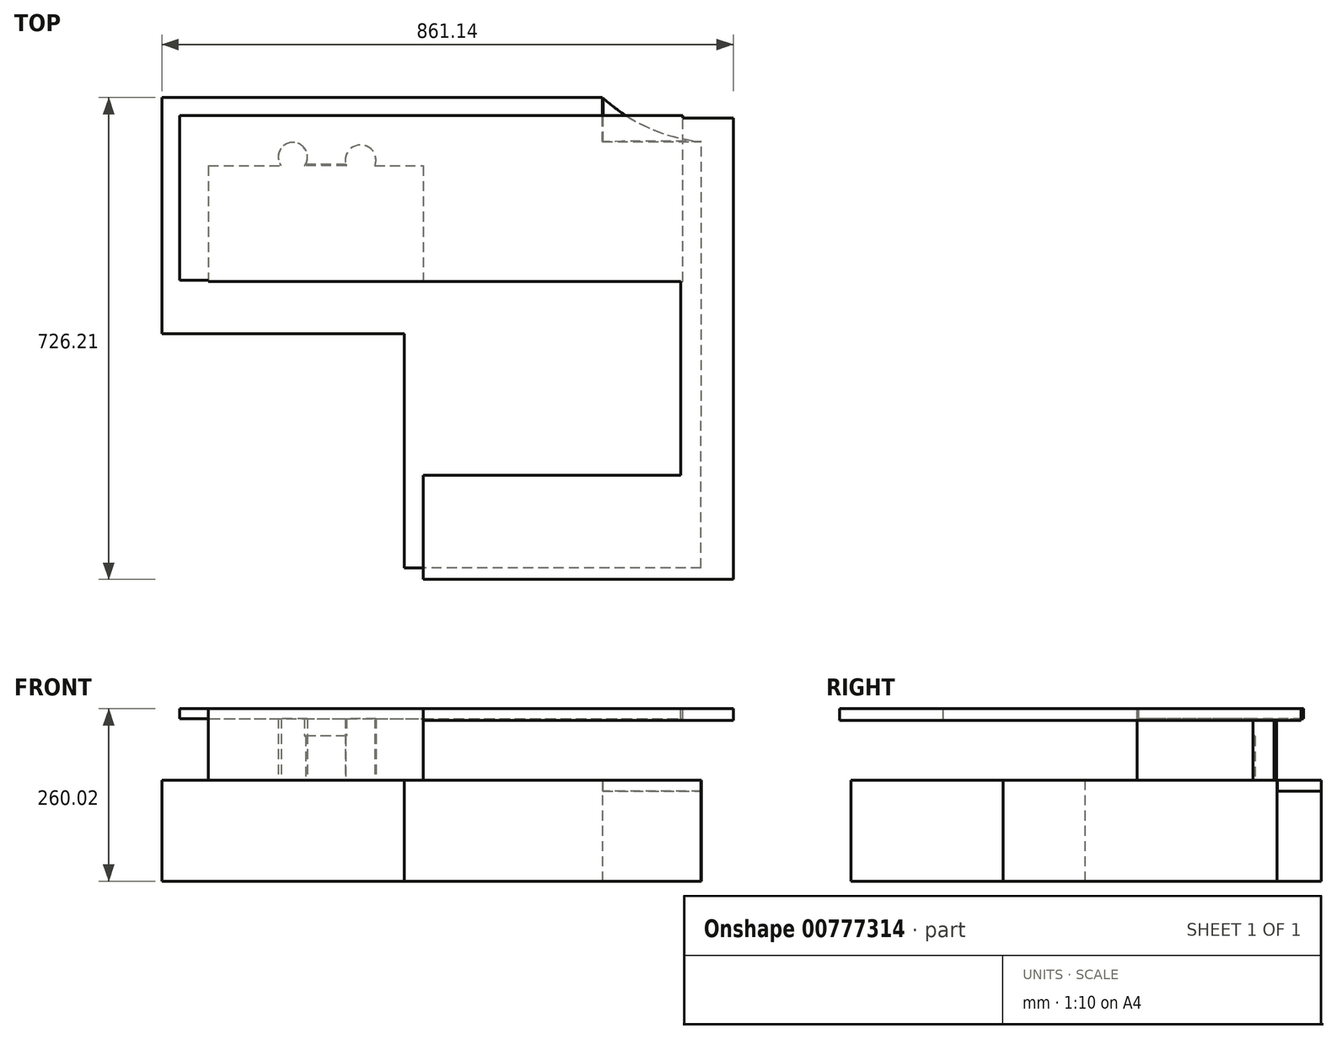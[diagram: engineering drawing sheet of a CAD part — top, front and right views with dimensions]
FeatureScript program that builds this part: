
annotation { "Feature Type Name" : "Feature", "Feature Type Description" : "" }
export const myFeature = defineFeature(function(context is Context, id is Id, definition is map)
    precondition{}
    {
        {
            var Q0;
            Q0=qCreatedBy(makeId("Top.planeOp"),FACE);
            var sketch = newSketch(context, id + "F0", { "sketchPlane" : qUnion([Q0])});
            skLineSegment(sketch, "E0.bottom", {"start": v(-322.14, 356.23) * mm, "end": v(-103.37, 356.23) * mm});
            skLineSegment(sketch, "E0.top", {"start": v(-322.14, 0) * mm, "end": v(-103.37, 0) * mm});
            skLineSegment(sketch, "E0.left", {"start": v(-322.14, 356.23) * mm, "end": v(-322.14, 0) * mm});
            skLineSegment(sketch, "E0.right", {"start": v(-103.37, 356.23) * mm, "end": v(-103.37, 0) * mm});
            skLineSegment(sketch, "E1.bottom", {"start": v(-103.37, 0) * mm, "end": v(193.48, 0) * mm});
            skLineSegment(sketch, "E1.top", {"start": v(-103.37, 139.09) * mm, "end": v(193.48, 139.09) * mm});
            skLineSegment(sketch, "E1.left", {"start": v(-103.37, 0) * mm, "end": v(-103.37, 139.09) * mm});
            skLineSegment(sketch, "E1.right", {"start": v(193.48, 0) * mm, "end": v(193.48, 139.09) * mm});
            skLineSegment(sketch, "E2.bottom", {"start": v(193.48, 0) * mm, "end": v(43.02, 0) * mm});
            skLineSegment(sketch, "E2.top", {"start": v(193.48, -352.95) * mm, "end": v(43.02, -352.95) * mm});
            skLineSegment(sketch, "E2.left", {"start": v(193.48, 0) * mm, "end": v(193.48, -352.95) * mm});
            skLineSegment(sketch, "E2.right", {"start": v(43.02, 0) * mm, "end": v(43.02, -352.95) * mm});
            skLineSegment(sketch, "E3.bottom", {"start": v(193.48, -352.95) * mm, "end": v(490.32, -352.95) * mm});
            skLineSegment(sketch, "E3.top", {"start": v(193.48, -123.6) * mm, "end": v(490.32, -123.6) * mm});
            skLineSegment(sketch, "E3.left", {"start": v(193.48, -352.95) * mm, "end": v(193.48, -123.6) * mm});
            skLineSegment(sketch, "E3.right", {"start": v(490.32, -352.95) * mm, "end": v(490.32, -123.6) * mm});
            skLineSegment(sketch, "E4.bottom", {"start": v(341.9, -123.6) * mm, "end": v(491.14, -123.6) * mm});
            skLineSegment(sketch, "E4.top", {"start": v(341.9, 289.54) * mm, "end": v(491.14, 289.54) * mm});
            skLineSegment(sketch, "E4.left", {"start": v(341.9, -123.6) * mm, "end": v(341.9, 289.54) * mm});
            skLineSegment(sketch, "E4.right", {"start": v(491.14, -123.6) * mm, "end": v(491.14, 289.54) * mm});
            skLineSegment(sketch, "E5.bottom", {"start": v(341.9, 289.54) * mm, "end": v(-103.37, 289.54) * mm});
            skLineSegment(sketch, "E5.top", {"start": v(341.9, 356.23) * mm, "end": v(-103.37, 356.23) * mm});
            skLineSegment(sketch, "E5.left", {"start": v(341.9, 289.54) * mm, "end": v(341.9, 356.23) * mm});
            skLineSegment(sketch, "E5.right", {"start": v(-103.37, 289.54) * mm, "end": v(-103.37, 356.23) * mm});
            skSolve(sketch);
        }
        {
            var Q0;
            {var subQ5=sQuery(id+"F0.wireOp",EDGE,"E1.top");Q0=makeQuery(id+"F0.imprint","IMPRINT",FACE,{"disambiguationData":[TD([[makeQuery(id+"F0.imprint","IMPRINT",EDGE,{"derivedFrom":subQ5}),1.0]])]});}
            var Q1;
            {var subQ0=sQuery(id+"F0.wireOp",EDGE,"E1.top");Q1=makeQuery(id+"F0.imprint","IMPRINT",FACE,{"disambiguationData":[TD([[makeQuery(id+"F0.imprint","IMPRINT",EDGE,{"derivedFrom":subQ0}),-1.0]])]});}
            var Q2;
            {var subQ4=sQuery(id+"F0.wireOp",EDGE,"E2.top");Q2=makeQuery(id+"F0.imprint","IMPRINT",FACE,{"disambiguationData":[TD([[makeQuery(id+"F0.imprint","IMPRINT",EDGE,{"derivedFrom":subQ4}),-1.0]])]});}
            var Q3;
            {var subQ3=sQuery(id+"F0.wireOp",EDGE,"E3.bottom");Q3=makeQuery(id+"F0.imprint","IMPRINT",FACE,{"disambiguationData":[TD([[makeQuery(id+"F0.imprint","IMPRINT",EDGE,{"derivedFrom":subQ3}),1.0]])]});}
            var Q4;
            {var subQ0=sQuery(id+"F0.wireOp",EDGE,"E4.bottom");Q4=makeQuery(id+"F0.imprint","IMPRINT",FACE,{"disambiguationData":[TD([[makeQuery(id+"F0.imprint","IMPRINT",EDGE,{"derivedFrom":subQ0}),1.0]])]});}
            var Q5;
            {var subQ2=sQuery(id+"F0.wireOp",EDGE,"E5.bottom");Q5=makeQuery(id+"F0.imprint","IMPRINT",FACE,{"disambiguationData":[TD([[makeQuery(id+"F0.imprint","IMPRINT",EDGE,{"derivedFrom":subQ2}),-1.0]])]});}
            var Q6;
            {var subQ4=sQuery(id+"F0.wireOp",EDGE,"E0.bottom");Q6=makeQuery(id+"F0.imprint","IMPRINT",FACE,{"disambiguationData":[TD([[makeQuery(id+"F0.imprint","IMPRINT",EDGE,{"derivedFrom":subQ4}),-1.0]])]});}
            extrude(context, id + "F1", {"entities" : qUnion([Q0, Q1, Q2, Q3, Q4, Q5, Q6]), "depth" : 152.4 * mm, "offsetDistance" : 25.4 * mm});
        }
        {
            var Q0;
            Q0=makeQuery(id+"F1.opExtrude","CAP_FACE",FACE,{"disambiguationData":[OSD([sQuery(id+"F0.wireOp",EDGE,"E0.bottom"),sQuery(id+"F0.wireOp",EDGE,"E0.top"),sQuery(id+"F0.wireOp",EDGE,"E0.left"),sQuery(id+"F0.wireOp",EDGE,"E1.bottom"),sQuery(id+"F0.wireOp",EDGE,"E2.top"),sQuery(id+"F0.wireOp",EDGE,"E2.right"),sQuery(id+"F0.wireOp",EDGE,"E3.bottom"),sQuery(id+"F0.wireOp",EDGE,"E3.right"),sQuery(id+"F0.wireOp",EDGE,"E4.bottom"),sQuery(id+"F0.wireOp",EDGE,"E4.top"),sQuery(id+"F0.wireOp",EDGE,"E4.right"),sQuery(id+"F0.wireOp",EDGE,"E5.top"),sQuery(id+"F0.wireOp",EDGE,"E5.left")])],"isStart":false});
            var sketch = newSketch(context, id + "F2", { "sketchPlane" : qUnion([Q0])});
            skSolve(sketch);
        }
        {
            var Q0;
            Q0=makeQuery(id+"F2.imprint","IMPRINT",FACE,{"disambiguationData":[TD([[makeQuery(id+"F2.imprint","IMPRINT",EDGE,{"derivedFrom":makeQuery(id+"F1.opExtrude","CAP_EDGE",EDGE,{"disambiguationData":[OSD([sQuery(id+"F0.wireOp",EDGE,"E0.left")])],"isStart":false})}),1.0]])]});
            var sketch = newSketch(context, id + "F3", { "sketchPlane" : qUnion([Q0])});
            skArc(sketch, "E6", {"start": v(342.5, 355.85) * mm, "mid": v(411.41, 310.78) * mm, "end": v(491.05, 289.87) * mm});
            skArc(sketch, "E7", {"start": v(491.05, 289.87) * mm, "mid": v(417.06, 290.34) * mm, "end": v(343.06, 289.87) * mm});
            skArc(sketch, "E8", {"start": v(343.06, 289.87) * mm, "mid": v(343.13, 322.86) * mm, "end": v(342.5, 355.85) * mm});
            skSolve(sketch);
        }
        {
            var Q0;
            Q0=makeQuery(id+"F3.imprint","IMPRINT",FACE,{"disambiguationData":[TD([[makeQuery(id+"F3.imprint","IMPRINT",EDGE,{"derivedFrom":sQuery(id+"F3.wireOp",EDGE,"E6")}),-1.0]])]});
            extrude(context, id + "F4", {"entities" : qUnion([Q0]), "oppositeDirection" : true, "depth" : 16.5 * mm, "offsetDistance" : 25.4 * mm});
        }
        {
            var Q0;
            Q0=makeQuery(id+"F2.imprint","IMPRINT",FACE,{"disambiguationData":[TD([[makeQuery(id+"F2.imprint","IMPRINT",EDGE,{"derivedFrom":makeQuery(id+"F1.opExtrude","CAP_EDGE",EDGE,{"disambiguationData":[OSD([sQuery(id+"F0.wireOp",EDGE,"E0.left")])],"isStart":false})}),1.0]])]});
            var sketch = newSketch(context, id + "F5", { "sketchPlane" : qUnion([Q0])});
            skCircle(sketch, "E9", {"center": v(-124.59, 266.64) * mm, "radius": 21.98 * mm});
            skPoint(sketch, "E9.first.point", {"position": v(-131.84, 245.89) * mm});
            skPoint(sketch, "E9.second.point", {"position": v(-104.8, 257.08) * mm});
            skPoint(sketch, "E9.third.point", {"position": v(-142.1, 253.34) * mm});
            skCircle(sketch, "E10", {"center": v(-22.56, 261.86) * mm, "radius": 23.06 * mm});
            skPoint(sketch, "E10.first.point", {"position": v(0, 266.64) * mm});
            skPoint(sketch, "E10.second.point", {"position": v(-45.12, 257.08) * mm});
            skPoint(sketch, "E10.third.point", {"position": v(0, 257.08) * mm});
            skLineSegment(sketch, "E11", {"start": v(-251.84, 253.34) * mm, "end": v(-142.1, 253.34) * mm});
            skLineSegment(sketch, "E12.bottom", {"start": v(-251.84, 253.34) * mm, "end": v(71.57, 253.34) * mm});
            skLineSegment(sketch, "E12.top", {"start": v(-251.84, 78.78) * mm, "end": v(71.57, 78.78) * mm});
            skLineSegment(sketch, "E12.left", {"start": v(-251.84, 253.34) * mm, "end": v(-251.84, 78.78) * mm});
            skLineSegment(sketch, "E12.right", {"start": v(71.57, 253.34) * mm, "end": v(71.57, 78.78) * mm});
            skLineSegment(sketch, "E13.bottom", {"start": v(71.57, 166.06) * mm, "end": v(268.86, 166.06) * mm});
            skLineSegment(sketch, "E13.top", {"start": v(71.57, 78.78) * mm, "end": v(268.86, 78.78) * mm});
            skLineSegment(sketch, "E13.left", {"start": v(71.57, 166.06) * mm, "end": v(71.57, 78.78) * mm});
            skLineSegment(sketch, "E13.right", {"start": v(268.86, 166.06) * mm, "end": v(268.86, 78.78) * mm});
            skSolve(sketch);
        }
        {
            var Q0;
            Q0=makeQuery(id+"F5.imprint","IMPRINT",FACE,{"disambiguationData":[TD([[makeQuery(id+"F5.imprint","IMPRINT",EDGE,{"derivedFrom":sQuery(id+"F5.wireOp",EDGE,"E12.top")}),1.0]])]});
            var Q1;
            {var subQ0=sQuery(id+"F5.wireOp",EDGE,"E12.bottom");var subQ1=sQuery(id+"F5.wireOp",EDGE,"E9");var subQ2=makeQuery(id+"F5.imprint","INTERSECT",VERTEX,{"disambiguationData":[OD(0.0)],"derivedFrom":[subQ1,subQ0]});Q1=makeQuery(id+"F5.imprint","IMPRINT",FACE,{"disambiguationData":[TD([[makeQuery(id+"F5.imprint","IMPRINT",EDGE,{"disambiguationData":[TD([[subQ2,1.0]])],"derivedFrom":subQ1}),1.0]])]});}
            var Q2;
            {var subQ0=sQuery(id+"F5.wireOp",EDGE,"E12.bottom");var subQ1=sQuery(id+"F5.wireOp",EDGE,"E10");var subQ2=makeQuery(id+"F5.imprint","INTERSECT",VERTEX,{"disambiguationData":[OD(0.0)],"derivedFrom":[subQ1,subQ0]});Q2=makeQuery(id+"F5.imprint","IMPRINT",FACE,{"disambiguationData":[TD([[makeQuery(id+"F5.imprint","IMPRINT",EDGE,{"disambiguationData":[TD([[subQ2,1.0]])],"derivedFrom":subQ1}),1.0]])]});}
            var Q3;
            {var subQ0=sQuery(id+"F5.wireOp",EDGE,"E12.bottom");var subQ1=sQuery(id+"F5.wireOp",EDGE,"E10");var subQ2=makeQuery(id+"F5.imprint","INTERSECT",VERTEX,{"disambiguationData":[OD(0.0)],"derivedFrom":[subQ1,subQ0]});Q3=makeQuery(id+"F5.imprint","IMPRINT",FACE,{"disambiguationData":[TD([[makeQuery(id+"F5.imprint","IMPRINT",EDGE,{"disambiguationData":[TD([[subQ2,-1.0]])],"derivedFrom":subQ1}),1.0]])]});}
            var Q4;
            {var subQ0=sQuery(id+"F5.wireOp",EDGE,"E12.bottom");var subQ1=sQuery(id+"F5.wireOp",EDGE,"E9");var subQ2=makeQuery(id+"F5.imprint","INTERSECT",VERTEX,{"disambiguationData":[OD(0.0)],"derivedFrom":[subQ1,subQ0]});Q4=makeQuery(id+"F5.imprint","IMPRINT",FACE,{"disambiguationData":[TD([[makeQuery(id+"F5.imprint","IMPRINT",EDGE,{"disambiguationData":[TD([[subQ2,-1.0]])],"derivedFrom":subQ1}),1.0]])]});}
            extrude(context, id + "F6", {"entities" : qUnion([Q0, Q1, Q2, Q3, Q4]), "operationType" : NewBodyOperationType.ADD, "depth" : 107.62 * mm, "offsetDistance" : 25.4 * mm});
        }
        {
            var Q0;
            Q0=makeQuery(id+"F6.opExtrude","CAP_FACE",FACE,{"disambiguationData":[OSD([sQuery(id+"F5.wireOp",EDGE,"E9"),sQuery(id+"F5.wireOp",EDGE,"E10"),sQuery(id+"F5.wireOp",EDGE,"E12.bottom"),sQuery(id+"F5.wireOp",EDGE,"E12.top"),sQuery(id+"F5.wireOp",EDGE,"E12.left"),sQuery(id+"F5.wireOp",EDGE,"E12.right"),sQuery(id+"F5.wireOp",EDGE,"E13.left")])],"isStart":false});
            var sketch = newSketch(context, id + "F7", { "sketchPlane" : qUnion([Q0])});
            skLineSegment(sketch, "E14.bottom", {"start": v(71.57, 78.78) * mm, "end": v(463.2, 78.78) * mm});
            skLineSegment(sketch, "E14.top", {"start": v(71.57, 329.25) * mm, "end": v(463.2, 329.25) * mm});
            skLineSegment(sketch, "E14.left", {"start": v(71.57, 78.78) * mm, "end": v(71.57, 329.25) * mm});
            skLineSegment(sketch, "E14.right", {"start": v(463.2, 78.78) * mm, "end": v(463.2, 329.25) * mm});
            skLineSegment(sketch, "E15.bottom", {"start": v(71.57, 329.25) * mm, "end": v(-251.84, 329.25) * mm});
            skLineSegment(sketch, "E15.top", {"start": v(71.57, 253.34) * mm, "end": v(-251.84, 253.34) * mm});
            skLineSegment(sketch, "E15.left", {"start": v(71.57, 329.25) * mm, "end": v(71.57, 253.34) * mm});
            skLineSegment(sketch, "E15.right", {"start": v(-251.84, 329.25) * mm, "end": v(-251.84, 253.34) * mm});
            skLineSegment(sketch, "E16.bottom", {"start": v(-251.84, 329.25) * mm, "end": v(-295.3, 329.25) * mm});
            skLineSegment(sketch, "E16.top", {"start": v(-251.84, 81.17) * mm, "end": v(-295.3, 81.17) * mm});
            skLineSegment(sketch, "E16.left", {"start": v(-251.84, 329.25) * mm, "end": v(-251.84, 81.17) * mm});
            skLineSegment(sketch, "E16.right", {"start": v(-295.3, 329.25) * mm, "end": v(-295.3, 81.17) * mm});
            skLineSegment(sketch, "E17.bottom", {"start": v(71.57, 78.78) * mm, "end": v(459.46, 78.78) * mm});
            skLineSegment(sketch, "E17.top", {"start": v(71.57, -213.4) * mm, "end": v(459.46, -213.4) * mm});
            skLineSegment(sketch, "E17.left", {"start": v(71.57, 78.78) * mm, "end": v(71.57, -213.4) * mm});
            skLineSegment(sketch, "E17.right", {"start": v(459.46, 78.78) * mm, "end": v(459.46, -213.4) * mm});
            skSolve(sketch);
        }
        {
            var Q0;
            Q0=makeQuery(id+"F7.imprint","IMPRINT",FACE,{"disambiguationData":[TD([[makeQuery(id+"F7.imprint","IMPRINT",EDGE,{"derivedFrom":sQuery(id+"F7.wireOp",EDGE,"E14.bottom")}),1.0]])]});
            var Q1;
            Q1=makeQuery(id+"F7.imprint","IMPRINT",FACE,{"disambiguationData":[TD([[makeQuery(id+"F7.imprint","IMPRINT",EDGE,{"derivedFrom":sQuery(id+"F7.wireOp",EDGE,"E17.bottom")}),-1.0]])]});
            var Q2;
            {var subQ6=sQuery(id+"F7.wireOp",EDGE,"E15.bottom");Q2=makeQuery(id+"F7.imprint","IMPRINT",FACE,{"disambiguationData":[TD([[makeQuery(id+"F7.imprint","IMPRINT",EDGE,{"derivedFrom":subQ6}),1.0]])]});}
            var Q3;
            {var subQ3=sQuery(id+"F7.wireOp",EDGE,"E16.bottom");Q3=makeQuery(id+"F7.imprint","IMPRINT",FACE,{"disambiguationData":[TD([[makeQuery(id+"F7.imprint","IMPRINT",EDGE,{"derivedFrom":subQ3}),1.0]])]});}
            extrude(context, id + "F8", {"entities" : qUnion([Q0, Q1, Q2, Q3]), "operationType" : NewBodyOperationType.ADD, "oppositeDirection" : true, "depth" : 15.06 * mm, "offsetDistance" : 25.4 * mm});
        }
        {
            var Q0;
            Q0=makeQuery(id+"F2.imprint","IMPRINT",FACE,{"disambiguationData":[TD([[makeQuery(id+"F2.imprint","IMPRINT",EDGE,{"derivedFrom":makeQuery(id+"F1.opExtrude","CAP_EDGE",EDGE,{"disambiguationData":[OSD([sQuery(id+"F0.wireOp",EDGE,"E0.left")])],"isStart":false})}),1.0]])]});
            var sketch = newSketch(context, id + "F9", { "sketchPlane" : qUnion([Q0])});
            skFitSpline(sketch, "E18", {"points": [v(487.83, -348.32) * mm, v(416.78, -212.63) * mm, v(491.76, -46.47) * mm, v(422.12, 95.85) * mm, v(489.36, 287.95) * mm, v(453.38, 286.78) * mm, v(394.04, 109.4) * mm, v(448.27, -46.35) * mm, v(381.23, -191.32) * mm, v(443.8, -349.95) * mm, v(487.83, -348.32) * mm]});
            skSolve(sketch);
        }
        {
            var Q0;
            Q0=sQuery(id+"F9.wireOp",EDGE,"E18");
            extrude(context, id + "F10", {"bodyType" : ToolBodyType.SURFACE, "surfaceEntities" : qUnion([Q0]), "depth" : 91.15 * mm, "offsetDistance" : 25.4 * mm});
        }
        {
            var Q0;
            {var subQ0=sQuery(id+"F5.wireOp",EDGE,"E10");var subQ1=sQuery(id+"F5.wireOp",EDGE,"E9");Q0=makeQuery(id+"F8.boolean.opBoolean","MERGE",FACE,{"derivedFrom":[makeQuery(id+"F6.opExtrude","CAP_FACE",FACE,{"disambiguationData":[OSD([subQ1,subQ0,sQuery(id+"F5.wireOp",EDGE,"E12.bottom"),sQuery(id+"F5.wireOp",EDGE,"E12.top"),sQuery(id+"F5.wireOp",EDGE,"E12.left"),sQuery(id+"F5.wireOp",EDGE,"E12.right"),sQuery(id+"F5.wireOp",EDGE,"E13.left")])],"isStart":false}),makeQuery(id+"F8.opExtrude","CAP_FACE",FACE,{"disambiguationData":[OSD([subQ1,subQ0,sQuery(id+"F7.wireOp",EDGE,"E14.bottom"),sQuery(id+"F7.wireOp",EDGE,"E14.top"),sQuery(id+"F7.wireOp",EDGE,"E14.left"),sQuery(id+"F7.wireOp",EDGE,"E14.right"),sQuery(id+"F7.wireOp",EDGE,"E15.bottom"),sQuery(id+"F7.wireOp",EDGE,"E15.top"),sQuery(id+"F7.wireOp",EDGE,"E16.bottom"),sQuery(id+"F7.wireOp",EDGE,"E16.top"),sQuery(id+"F7.wireOp",EDGE,"E16.left"),sQuery(id+"F7.wireOp",EDGE,"E16.right"),sQuery(id+"F7.wireOp",EDGE,"E17.top"),sQuery(id+"F7.wireOp",EDGE,"E17.left"),sQuery(id+"F7.wireOp",EDGE,"E17.right")])],"isStart":true})]});}
            var sketch = newSketch(context, id + "F11", { "sketchPlane" : qUnion([Q0])});
            skLineSegment(sketch, "E19.bottom", {"start": v(71.57, -213.4) * mm, "end": v(459.68, -213.4) * mm});
            skLineSegment(sketch, "E19.top", {"start": v(71.57, -369.98) * mm, "end": v(459.68, -369.98) * mm});
            skLineSegment(sketch, "E19.left", {"start": v(71.57, -213.4) * mm, "end": v(71.57, -369.98) * mm});
            skLineSegment(sketch, "E19.right", {"start": v(459.68, -213.4) * mm, "end": v(459.68, -369.98) * mm});
            skLineSegment(sketch, "E20.bottom", {"start": v(459.68, -369.98) * mm, "end": v(539, -369.98) * mm});
            skLineSegment(sketch, "E20.top", {"start": v(459.68, 325.34) * mm, "end": v(539, 325.34) * mm});
            skLineSegment(sketch, "E20.left", {"start": v(459.68, -369.98) * mm, "end": v(459.68, 325.34) * mm});
            skLineSegment(sketch, "E20.right", {"start": v(539, -369.98) * mm, "end": v(539, 325.34) * mm});
            skSolve(sketch);
        }
        {
            var Q0;
            {var subQ6=sQuery(id+"F11.wireOp",EDGE,"E20.bottom");Q0=makeQuery(id+"F11.imprint","IMPRINT",FACE,{"disambiguationData":[TD([[makeQuery(id+"F11.imprint","IMPRINT",EDGE,{"derivedFrom":subQ6}),1.0]])]});}
            var Q1;
            {var subQ1=sQuery(id+"F11.wireOp",EDGE,"E19.top");Q1=makeQuery(id+"F11.imprint","IMPRINT",FACE,{"disambiguationData":[TD([[makeQuery(id+"F11.imprint","IMPRINT",EDGE,{"derivedFrom":subQ1}),1.0]])]});}
            extrude(context, id + "F12", {"entities" : qUnion([Q0, Q1]), "operationType" : NewBodyOperationType.ADD, "oppositeDirection" : true, "depth" : 17.52 * mm, "offsetDistance" : 25.4 * mm});
        }
        {
            var Q0;
            {var subQ0=sQuery(id+"F5.wireOp",EDGE,"E12.bottom");Q0=makeQuery(id+"F6.opExtrude","SWEPT_FACE",FACE,{"disambiguationData":[OSD([subQ0]),TDD([makeQuery(id+"F5.imprint","IMPRINT",EDGE,{"disambiguationData":[TD([[makeQuery(id+"F5.imprint","INTERSECT",VERTEX,{"disambiguationData":[OD(1.0)],"derivedFrom":[sQuery(id+"F5.wireOp",EDGE,"E9"),subQ0]}),-1.0]])],"derivedFrom":subQ0})])]});}
            var sketch = newSketch(context, id + "F13", { "sketchPlane" : qUnion([Q0])});
            skLineSegment(sketch, "E21.bottom", {"start": v(43.99, 218.58) * mm, "end": v(107.08, 218.58) * mm});
            skLineSegment(sketch, "E21.top", {"start": v(43.99, 152.4) * mm, "end": v(107.08, 152.4) * mm});
            skLineSegment(sketch, "E21.left", {"start": v(43.99, 218.58) * mm, "end": v(43.99, 152.4) * mm});
            skLineSegment(sketch, "E21.right", {"start": v(107.08, 218.58) * mm, "end": v(107.08, 152.4) * mm});
            skSolve(sketch);
        }
        {
            var Q0;
            Q0=makeQuery(id+"F13.imprint","IMPRINT",FACE,{"disambiguationData":[TD([[makeQuery(id+"F13.imprint","IMPRINT",EDGE,{"derivedFrom":sQuery(id+"F13.wireOp",EDGE,"E21.bottom")}),-1.0]])]});
            var sketch = newSketch(context, id + "F14", { "sketchPlane" : qUnion([Q0])});
            skLineSegment(sketch, "E22", {"start": v(73.94, 217.83) * mm, "end": v(73.94, 153.96) * mm});
            skSolve(sketch);
        }
        {
            var Q0;
            Q0 = qSketchRegion(id + "F13", true);
            var Q1;
            Q1=makeQuery(id+"F14.imprint","IMPRINT",FACE,{"disambiguationData":[TD([[makeQuery(id+"F14.imprint","IMPRINT",EDGE,{"derivedFrom":makeQuery(id+"F13.imprint","IMPRINT",EDGE,{"derivedFrom":sQuery(id+"F13.wireOp",EDGE,"E21.bottom")})}),-1.0]])]});
            extrude(context, id + "F15", {"entities" : qUnion([Q0, Q1]), "operationType" : NewBodyOperationType.ADD, "depth" : 2.96 * mm, "offsetDistance" : 25.4 * mm});
        }
    });
